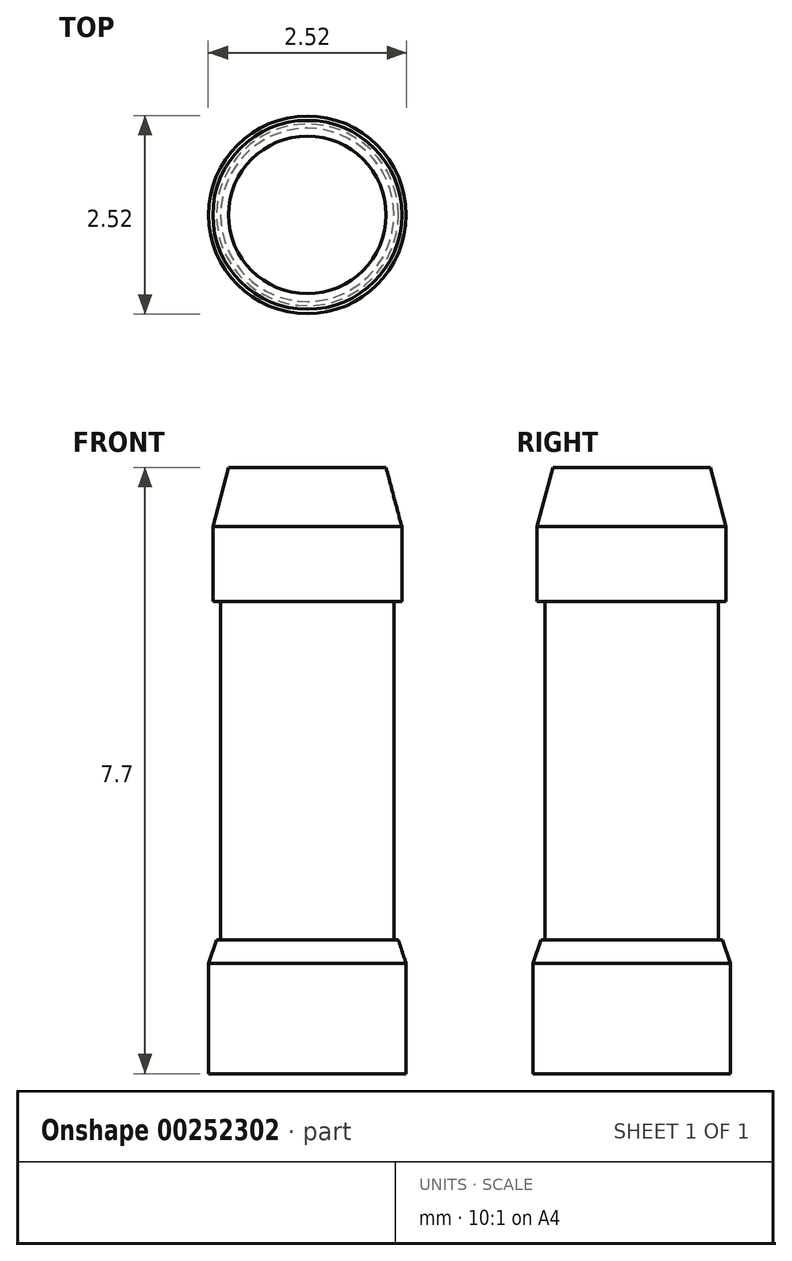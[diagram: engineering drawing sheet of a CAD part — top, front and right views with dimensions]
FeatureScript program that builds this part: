
annotation { "Feature Type Name" : "Feature", "Feature Type Description" : "" }
export const myFeature = defineFeature(function(context is Context, id is Id, definition is map)
    precondition{}
    {
        {
            var Q0;
            Q0=qCreatedBy(makeId("Front.planeOp"),FACE);
            var sketch = newSketch(context, id + "F0", { "sketchPlane" : qUnion([Q0])});
            skLineSegment(sketch, "E0", {"start": v(0, 7.7) * mm, "end": v(1.2, 7.7) * mm});
            skLineSegment(sketch, "E1", {"start": v(1.2, 7.7) * mm, "end": v(1.2, 6) * mm});
            skLineSegment(sketch, "E2", {"start": v(1.1, 6) * mm, "end": v(1.1, 1.7) * mm});
            skLineSegment(sketch, "E3", {"start": v(1.1, 1.7) * mm, "end": v(1.25, 1.7) * mm});
            skLineSegment(sketch, "E4", {"start": v(1.25, 1.7) * mm, "end": v(1.25, 0) * mm});
            skLineSegment(sketch, "E5", {"start": v(1.25, 0) * mm, "end": v(0, 0) * mm});
            skLineSegment(sketch, "E6", {"start": v(1.2, 6) * mm, "end": v(1.1, 6) * mm});
            skLineSegment(sketch, "E7", {"start": v(0, 7.7) * mm, "end": v(0, 0) * mm});
            skSolve(sketch);
        }
        {
            var Q0;
            Q0=makeQuery(id+"F0.imprint","IMPRINT",FACE,{"disambiguationData":[TD([[makeQuery(id+"F0.imprint","IMPRINT",EDGE,{"derivedFrom":sQuery(id+"F0.wireOp",EDGE,"E0")}),-1.0]])]});
            var Q1;
            Q1=sQuery(id+"F0.wireOp",EDGE,"E7");
            revolve(context, id + "F1", {"entities" : qUnion([Q0]), "axis" : qUnion([Q1]), "revolveType" : RevolveType.FULL});
        }
        {
            var Q0;
            Q0=makeQuery(id+"F1.opRevolve","SWEPT_EDGE",EDGE,{"disambiguationData":[OSD([sQuery(id+"F0.wireOp",EDGE,"E0"),sQuery(id+"F0.wireOp",EDGE,"E1")])]});
            chamfer(context, id + "F2", {"entities" : qUnion([Q0]), "chamferType" : ChamferType.TWO_OFFSETS, "width1" : .2 * mm, "oppositeDirection" : false, "width2" : .75 * mm, "tangentPropagation" : true});
        }
        {
            var Q0;
            Q0=makeQuery(id+"F1.opRevolve","SWEPT_EDGE",EDGE,{"disambiguationData":[OSD([sQuery(id+"F0.wireOp",EDGE,"E3"),sQuery(id+"F0.wireOp",EDGE,"E4")])]});
            chamfer(context, id + "F3", {"entities" : qUnion([Q0]), "chamferType" : ChamferType.TWO_OFFSETS, "width1" : .1 * mm, "oppositeDirection" : false, "width2" : .3 * mm, "tangentPropagation" : true});
        }
    });
